# Revit family: Boiler-Gas-Weil-McLain-SVF_1500-3000
name_source: partatom
category: Mechanical Equipment
revit_build: Autodesk Revit 2016 (Build: 20150714_1515(x64)
units: mm (PartAtom-declared; Revit-internal decimal feet)

## family parameters
Always vertical = Yes
Cut with Voids When Loaded = No
OmniClass Number = 23.75.10.11.14
OmniClass Title = Hot Water Heat Generators
Part Type = Normal
Room Calculation Point = No
Round Connector Dimension = Use Diameter
Shared = No
Work Plane-Based = Yes

## types (8) — shared parameters
Assembly Code = D3020100
Boiler Return Water Diameter = 3"
Boiler Supply Water Diameter = 3"
Condensate Drain Connection Diameter = 1"
Default Elevation = 0' - 0"
Frame Accent Material = Plastic - WeilMcLain - Black
Frame Finish = Metal - WeilMcLain - Gray
Frequency = 60 Hz
Gas Connection Diameter = 2"
Gas Connection Type = Female NPT
Height = 6' - 7 1/8"
Keynote = 23 52 00
Manufacturer = Weil-McLain
Number of Poles = 1
Operating Temperature = 40 - 120 F
Product Page URL = https://www.weil-mclain.com
Screen Material = Plastic - WeilMcLain - Blue
Standards Conformance = ASME  ;  AHRI  ;  CSA
Type Comments = No Side Clearance. Side-by-Side install capable.
URL = https://www.weil-mclain.com
Water Connection Type = Class 150 ASME Flange
Width = 2' - 11 3/16"

## per-type parameters (varying)
| type | CondensateCL | CondensateLocate | Dead Weight | Description | Flue Diameter | Flue Inset | Flue Locate | FlueHolderDia | Fuel Type | Full Load Current | Length | Model | Net AHRI MBH | Operating Weight | Phase | Product Name | Supply Air Connection Diameter | Tank Capacity | Thermal Efficiency | Total Heating Capacity | Voltage |
| SVF1500 NG | 0' - 4 15/16" | 0' - 11 15/16" | 2020 | Weil-McLain Commercial NG Gas Boiler - SVF1500 as Specified | 8" | 0' - 9 3/16" | 6' - 4 15/32" | 0' - 9 1/2" | Natural Gas | 23 A | 7' - 0 5/16" | SVF1500 | 1259.0 Btu/h | 3000 | 1 | SVF1500 Boiler | 8" | 118 gal | 96.5 | 1448.0 Btu/h | 120 V |
| SVF2000 NG | 0' - 4 15/16" | 0' - 11 15/16" | 2020 | Weil-McLain Commercial NG Gas Boiler - SVF2000 as Specified | 8" | 0' - 9 3/16" | 6' - 4 15/32" | 0' - 9 1/2" | Natural Gas | 23 A | 7' - 0 5/16" | SVF2000 | 1672.0 Btu/h | 3000 | 1 | SVF2000 Boiler | 8" | 118 gal | 96.2 | 1923.0 Btu/h | 120 V |
| SVF2500 NG | 0' - 4" | 0' - 10 1/4" | 2350 | Weil-McLain Commercial NG Gas Boiler - SVF2500 as Specified | 10" | 0' - 8 9/16" | 6' - 5 9/16" | 0' - 11 1/2" | Natural Gas | 16 A | 7' - 2 15/16" | SVF2500 | 2104.0 Btu/h | 3590 | 3 | SVF2500 Boiler | 10" | 149 gal | 96.8 | 2419.0 Btu/h | 208 V |
| SVF3000 NG | 0' - 4" | 0' - 10 1/4" | 2350 | Weil-McLain Commercial NG Gas Boiler - SVF3000 as Specified | 10" | 0' - 8 9/16" | 6' - 5 9/16" | 0' - 11 1/2" | Natural Gas | 16 A | 7' - 2 15/16" | SVF3000 | 2499.0 Btu/h | 3590 | 3 | SVF3000 Boiler | 10" | 149 gal | 0 | 2874.0 Btu/h | 208 V |
| SVF1500 LP | 0' - 4 15/16" | 0' - 11 15/16" | 2020 | Weil-McLain Commercial LP Gas Boiler - SVF1500 as Specified | 8" | 0' - 9 3/16" | 6' - 4 15/32" | 0' - 9 1/2" | Liquid Propane | 23 A | 7' - 0 5/16" | SVF1500 | 1259.0 Btu/h | 3000 | 1 | SVF1500 Boiler | 8" | 118 gal | 96.5 | 1448.0 Btu/h | 120 V |
| SVF2000 LP | 0' - 4 15/16" | 0' - 11 15/16" | 2020 | Weil-McLain Commercial LP Gas Boiler - SVF2000 as Specified | 8" | 0' - 9 3/16" | 6' - 4 15/32" | 0' - 9 1/2" | Liquid Propane | 23 A | 7' - 0 5/16" | SVF2000 | 1672.0 Btu/h | 3000 | 1 | SVF2000 Boiler | 8" | 118 gal | 96.2 | 1923.0 Btu/h | 120 V |
| SVF2500 LP | 0' - 4" | 0' - 10 1/4" | 2350 | Weil-McLain Commercial LP Gas Boiler - SVF2500 as Specified | 10" | 0' - 8 9/16" | 6' - 5 9/16" | 0' - 11 1/2" | Liquid Propane | 16 A | 7' - 2 15/16" | SVF2500 | 2104.0 Btu/h | 3590 | 3 | SVF2500 Boiler | 10" | 149 gal | 96.8 | 2419.0 Btu/h | 208 V |
| SVF3000 LP | 0' - 4" | 0' - 10 1/4" | 2350 | Weil-McLain Commercial LP Gas Boiler - SVF3000 as Specified | 10" | 0' - 8 9/16" | 6' - 5 9/16" | 0' - 11 1/2" | Liquid Propane | 16 A | 7' - 2 15/16" | SVF3000 | 2499.0 Btu/h | 3590 | 3 | SVF3000 Boiler | 10" | 149 gal | 0 | 2874.0 Btu/h | 208 V |

## geometry (parser evidence)
native form markers: Sweep x2
no freeform markers — native parametric forms only
